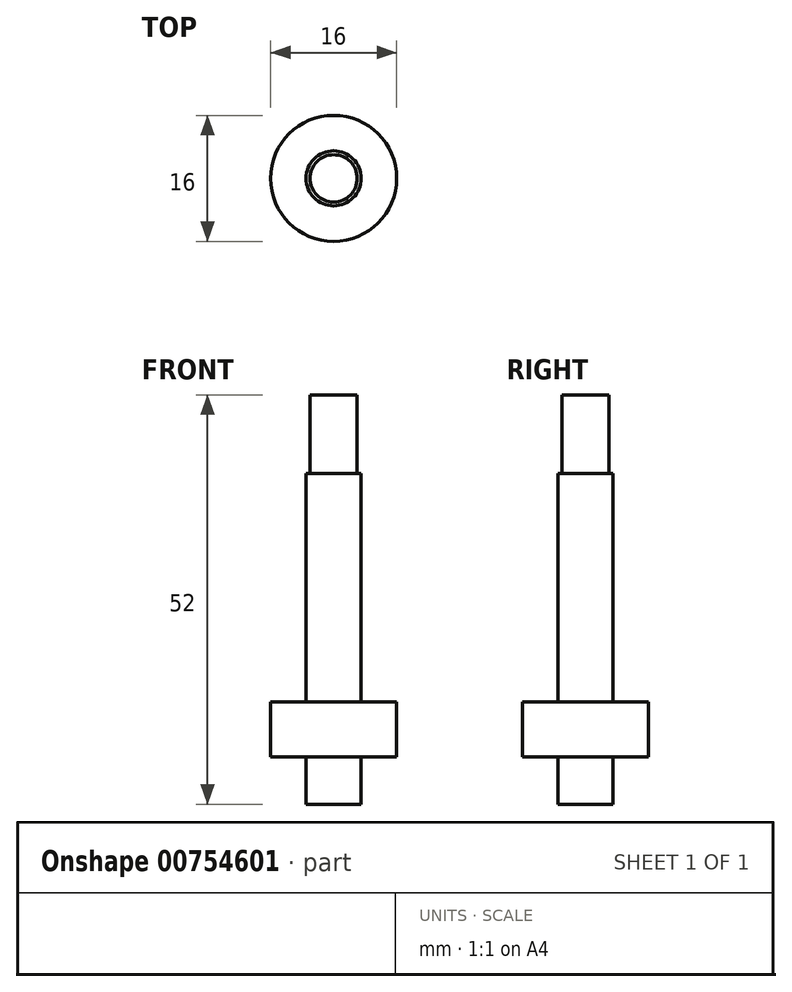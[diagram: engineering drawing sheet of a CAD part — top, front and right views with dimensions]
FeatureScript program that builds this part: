
annotation { "Feature Type Name" : "Feature", "Feature Type Description" : "" }
export const myFeature = defineFeature(function(context is Context, id is Id, definition is map)
    precondition{}
    {
        {
            var Q0;
            Q0=qCreatedBy(makeId("Top.planeOp"),FACE);
            var sketch = newSketch(context, id + "F0", { "sketchPlane" : qUnion([Q0])});
            skCircle(sketch, "E0", {"center": v(0, 0) * mm, "radius": 3.5 * mm});
            skSolve(sketch);
        }
        {
            var Q0;
            Q0 = qSketchRegion(id + "F0", true);
            extrude(context, id + "F1", {"entities" : qUnion([Q0]), "depth" : 6 * mm, "offsetDistance" : 25 * mm});
        }
        {
            var Q0;
            Q0=makeQuery(id+"F1.opExtrude","CAP_FACE",FACE,{"disambiguationData":[OSD([sQuery(id+"F0.wireOp",EDGE,"E0")])],"isStart":false});
            var sketch = newSketch(context, id + "F2", { "sketchPlane" : qUnion([Q0])});
            skCircle(sketch, "E1", {"center": v(0, 0) * mm, "radius": 8 * mm});
            skSolve(sketch);
        }
        {
            var Q0;
            Q0 = qSketchRegion(id + "F2", true);
            extrude(context, id + "F3", {"entities" : qUnion([Q0]), "operationType" : NewBodyOperationType.ADD, "depth" : 7 * mm, "offsetDistance" : 25 * mm});
        }
        {
            var Q0;
            Q0=makeQuery(id+"F3.opExtrude","CAP_FACE",FACE,{"disambiguationData":[OSD([sQuery(id+"F2.wireOp",EDGE,"E1")])],"isStart":false});
            var sketch = newSketch(context, id + "F4", { "sketchPlane" : qUnion([Q0])});
            skCircle(sketch, "E2", {"center": v(0, 0) * mm, "radius": 3.5 * mm});
            skSolve(sketch);
        }
        {
            var Q0;
            Q0 = qSketchRegion(id + "F4", true);
            extrude(context, id + "F5", {"entities" : qUnion([Q0]), "operationType" : NewBodyOperationType.ADD, "depth" : 29 * mm, "offsetDistance" : 25 * mm});
        }
        {
            var Q0;
            Q0=makeQuery(id+"F5.opExtrude","CAP_FACE",FACE,{"disambiguationData":[OSD([sQuery(id+"F4.wireOp",EDGE,"E2")])],"isStart":false});
            var sketch = newSketch(context, id + "F6", { "sketchPlane" : qUnion([Q0])});
            skCircle(sketch, "E3", {"center": v(0, 0) * mm, "radius": 3 * mm});
            skSolve(sketch);
        }
        {
            var Q0;
            Q0 = qSketchRegion(id + "F6", true);
            extrude(context, id + "F7", {"entities" : qUnion([Q0]), "operationType" : NewBodyOperationType.ADD, "depth" : 10 * mm, "offsetDistance" : 25 * mm});
        }
    });
